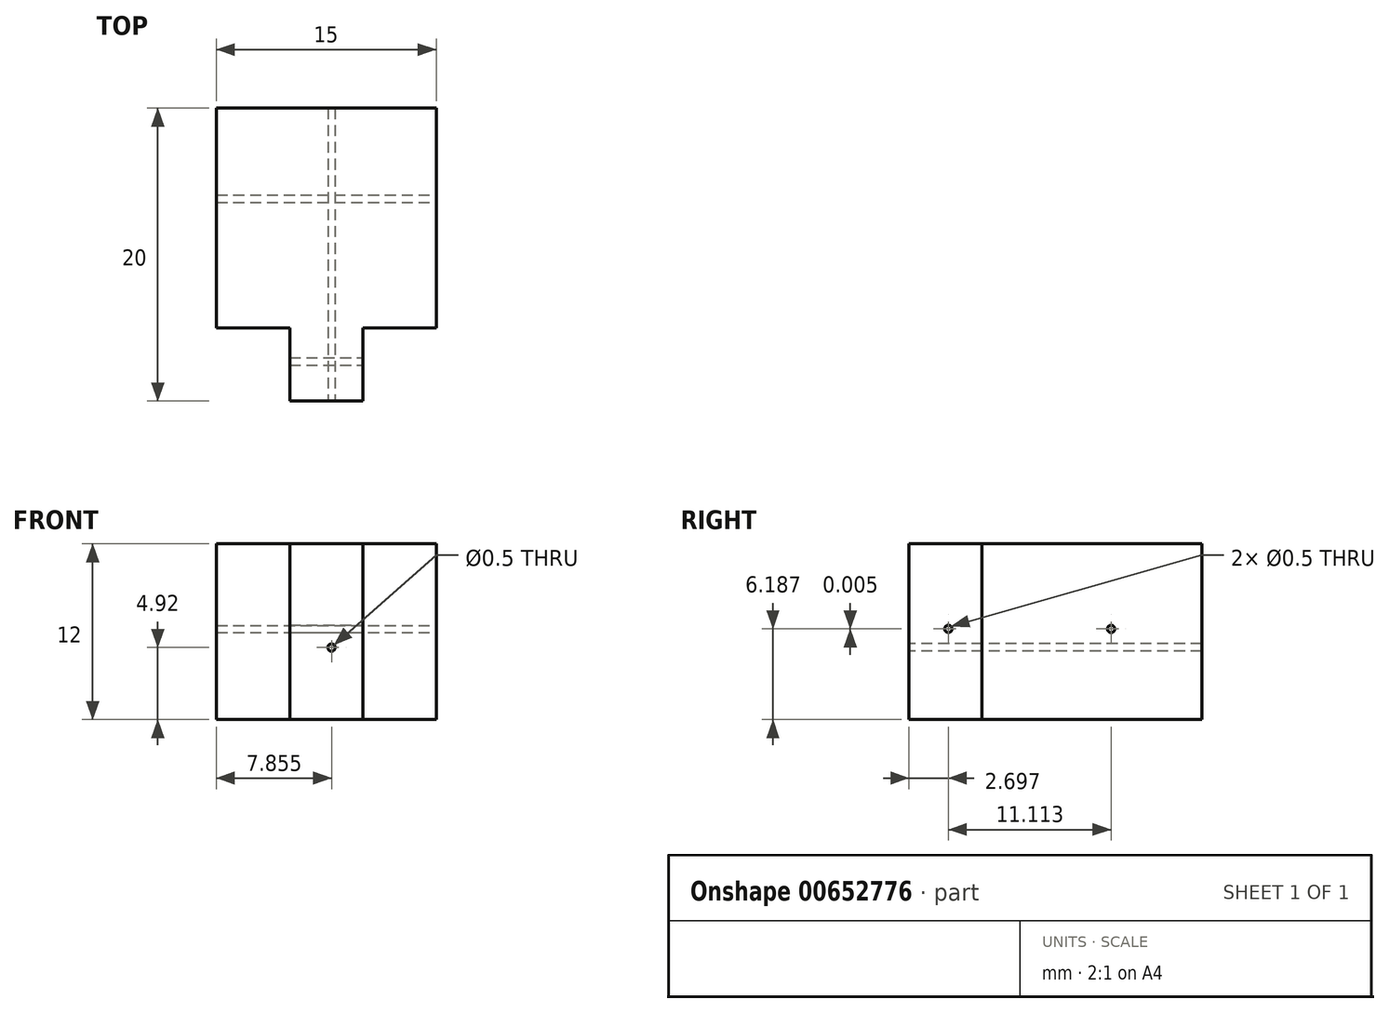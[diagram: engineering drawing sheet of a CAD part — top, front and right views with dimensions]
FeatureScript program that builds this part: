
annotation { "Feature Type Name" : "Feature", "Feature Type Description" : "" }
export const myFeature = defineFeature(function(context is Context, id is Id, definition is map)
    precondition{}
    {
        {
            var Q0;
            Q0=qCreatedBy(makeId("Top.planeOp"),FACE);
            var sketch = newSketch(context, id + "F0", { "sketchPlane" : qUnion([Q0])});
            skLineSegment(sketch, "E0.bottom", {"start": v(-15, 20) * mm, "end": v(0, 20) * mm});
            skLineSegment(sketch, "E0.left", {"start": v(-15, 20) * mm, "end": v(-15, 5) * mm});
            skLineSegment(sketch, "E0.right", {"start": v(0, 20) * mm, "end": v(0, 5) * mm});
            skLineSegment(sketch, "E1.top", {"start": v(-10, 0) * mm, "end": v(-5, 0) * mm});
            skLineSegment(sketch, "E1.left", {"start": v(-10, 5) * mm, "end": v(-10, 0) * mm});
            skLineSegment(sketch, "E1.right", {"start": v(-5, 5) * mm, "end": v(-5, 0) * mm});
            skLineSegment(sketch, "E2", {"start": v(-10, 5) * mm, "end": v(-15, 5) * mm});
            skLineSegment(sketch, "E3", {"start": v(-5, 5) * mm, "end": v(0, 5) * mm});
            skSolve(sketch);
        }
        {
            var Q0;
            Q0 = qSketchRegion(id + "F0", true);
            extrude(context, id + "F1", {"entities" : qUnion([Q0]), "depth" : 12 * mm, "offsetDistance" : 25 * mm});
        }
        {
            var Q0;
            Q0=qCreatedBy(makeId("Right.planeOp"),FACE);
            var sketch = newSketch(context, id + "F2", { "sketchPlane" : qUnion([Q0])});
            skCircle(sketch, "E4", {"center": v(13.81, 6.19) * mm, "radius": 0.25 * mm});
            skSolve(sketch);
        }
        {
            var Q0;
            Q0 = qSketchRegion(id + "F2", true);
            extrude(context, id + "F3", {"entities" : qUnion([Q0]), "operationType" : NewBodyOperationType.REMOVE, "oppositeDirection" : true, "depth" : 52.1 * mm, "offsetDistance" : 25 * mm});
        }
        {
            var Q0;
            Q0=qCreatedBy(makeId("Front.planeOp"),FACE);
            var sketch = newSketch(context, id + "F4", { "sketchPlane" : qUnion([Q0])});
            skCircle(sketch, "E5", {"center": v(-7.14, 4.92) * mm, "radius": 0.25 * mm});
            skSolve(sketch);
        }
        {
            var Q0;
            Q0 = qSketchRegion(id + "F4", true);
            extrude(context, id + "F5", {"entities" : qUnion([Q0]), "operationType" : NewBodyOperationType.REMOVE, "oppositeDirection" : true, "depth" : 44 * mm, "offsetDistance" : 25 * mm});
        }
        {
            var Q0;
            Q0=qCreatedBy(makeId("Right.planeOp"),FACE);
            var sketch = newSketch(context, id + "F6", { "sketchPlane" : qUnion([Q0])});
            skCircle(sketch, "E6", {"center": v(2.7, 6.2) * mm, "radius": 0.25 * mm});
            skSolve(sketch);
        }
        {
            var Q0;
            Q0 = qSketchRegion(id + "F6", true);
            extrude(context, id + "F7", {"entities" : qUnion([Q0]), "operationType" : NewBodyOperationType.REMOVE, "oppositeDirection" : true, "depth" : 57 * mm, "offsetDistance" : 25 * mm});
        }
    });
